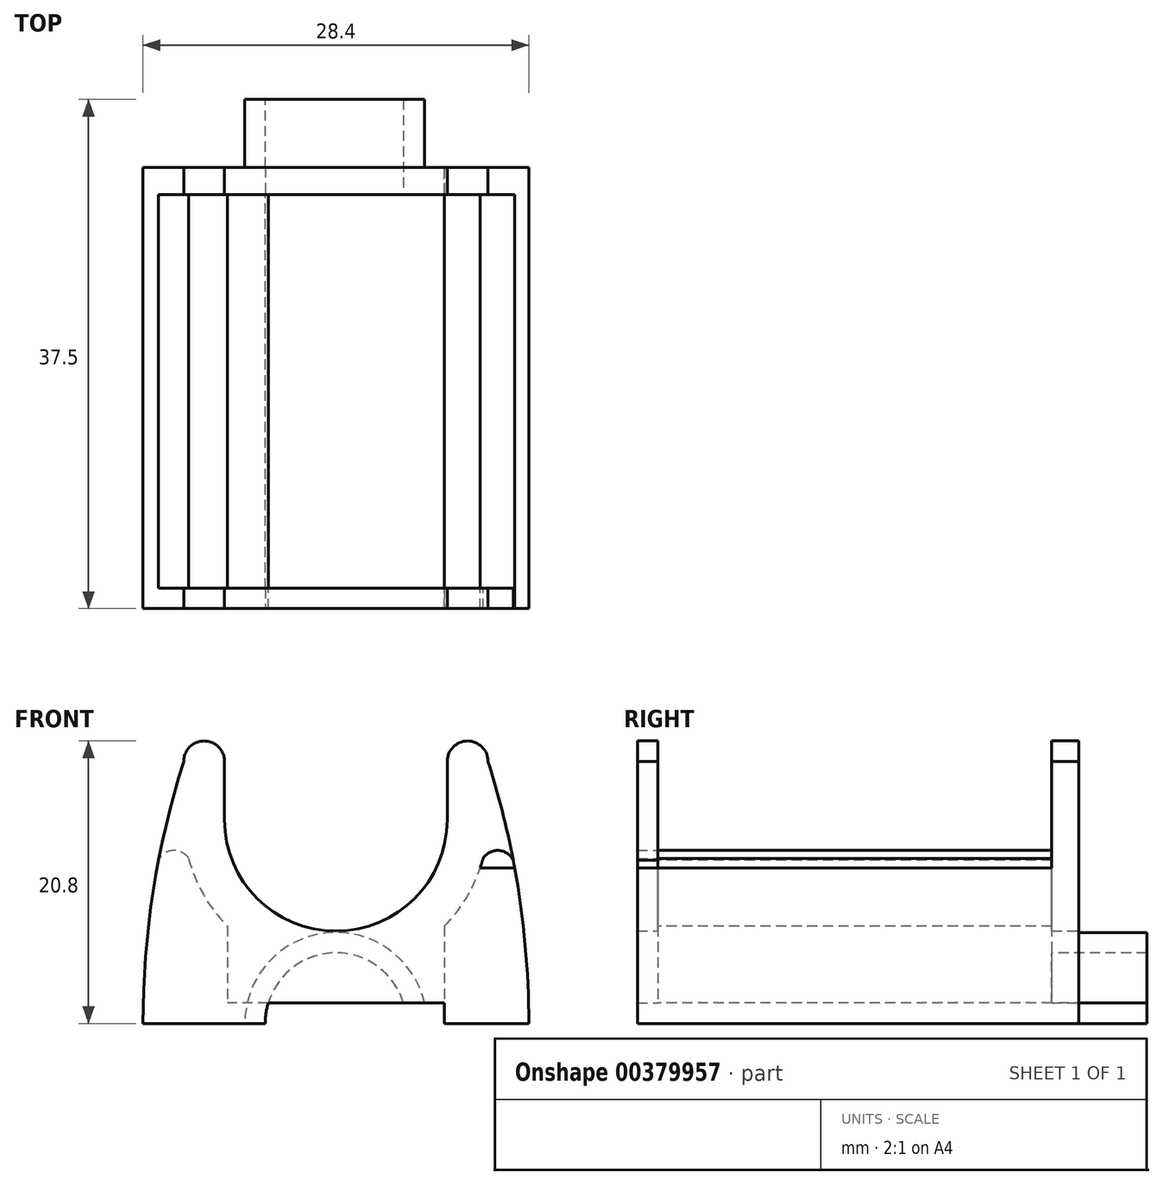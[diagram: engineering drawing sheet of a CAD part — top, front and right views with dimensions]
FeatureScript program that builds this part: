
annotation { "Feature Type Name" : "Feature", "Feature Type Description" : "" }
export const myFeature = defineFeature(function(context is Context, id is Id, definition is map)
    precondition{}
    {
        {
            var Q0;
            Q0=qCreatedBy(makeId("Front.planeOp"),FACE);
            cPlane(context, id + "F0", {"entities" : qUnion([Q0]), "cplaneType" : CPlaneType.OFFSET, "offset" : 6 * mm, "width" : 150 * mm, "height" : 150 * mm});
        }
        {
            var Q0;
            Q0=qCreatedBy(makeId("Front.planeOp"),FACE);
            cPlane(context, id + "F1", {"entities" : qUnion([Q0]), "cplaneType" : CPlaneType.OFFSET, "offset" : 37 * mm, "width" : 150 * mm, "height" : 150 * mm});
        }
        {
            var Q0;
            Q0=qCreatedBy(makeId("Top.planeOp"),FACE);
            var sketch = newSketch(context, id + "F2", { "sketchPlane" : qUnion([Q0])});
            skLineSegment(sketch, "E0.0", {"start": v(-8.05, -8) * mm, "end": v(-8.05, -37) * mm, "construction": true});
            skLineSegment(sketch, "E1.0", {"start": v(7.95, -8) * mm, "end": v(7.95, -37) * mm, "construction": true});
            skLineSegment(sketch, "E2.0", {"start": v(8.15, -8) * mm, "end": v(-8.25, -8) * mm, "construction": true});
            skLineSegment(sketch, "E3.0", {"start": v(8.15, -37) * mm, "end": v(-8.25, -37) * mm, "construction": true});
            skCircle(sketch, "E4", {"center": v(0, 0) * mm, "radius": 0.5 * mm, "construction": true});
            skLineSegment(sketch, "E5", {"start": v(-8.05, -22.5) * mm, "end": v(8.15, -8) * mm, "construction": true});
            skLineSegment(sketch, "E6", {"start": v(-8.05, -8) * mm, "end": v(7.95, -22.5) * mm, "construction": true});
            skLineSegment(sketch, "E7", {"start": v(7.95, -22.5) * mm, "end": v(-8.05, -37) * mm, "construction": true});
            skLineSegment(sketch, "E8", {"start": v(8.15, -37) * mm, "end": v(-8.05, -22.5) * mm, "construction": true});
            skCircle(sketch, "E9", {"center": v(0, -15.3) * mm, "radius": 1.38 * mm});
            skCircle(sketch, "E10", {"center": v(0, -29.7) * mm, "radius": 1.38 * mm});
            skSolve(sketch);
        }
        {
            var Q0;
            Q0=qCreatedBy(id+"F0.planeOp",FACE);
            var sketch = newSketch(context, id + "F3", { "sketchPlane" : qUnion([Q0])});
            skCircle(sketch, "E11", {"center": v(0, 0) * mm, "radius": 0.5 * mm, "construction": true});
            skArc(sketch, "E12.0", {"start": v(6.7, 8) * mm, "mid": v(0, 14.7) * mm, "end": v(-6.7, 8) * mm});
            skArc(sketch, "E13.0", {"start": v(5.2, 8) * mm, "mid": v(0, 13.2) * mm, "end": v(-5.2, 8) * mm});
            skLineSegment(sketch, "E14.bottom", {"start": v(14.2, 8) * mm, "end": v(-14.2, 8) * mm});
            skLineSegment(sketch, "E15", {"start": v(0, 23) * mm, "end": v(0, 8) * mm, "construction": true});
            skLineSegment(sketch, "E16", {"start": v(-8, 15.16) * mm, "end": v(-8, 8) * mm});
            skLineSegment(sketch, "E17.MirrorCS", {"start": v(8, 15.16) * mm, "end": v(8, 8) * mm});
            skLineSegment(sketch, "E18", {"start": v(-11.2, 23) * mm, "end": v(-11.2, 27.3) * mm});
            skLineSegment(sketch, "E19.MirrorCS", {"start": v(11.2, 23) * mm, "end": v(11.2, 27.3) * mm});
            skArc(sketch, "E20", {"start": v(-11.2, 23) * mm, "mid": v(-10.37, 18.77) * mm, "end": v(-8, 15.16) * mm});
            skLineSegment(sketch, "E21.0", {"start": v(8.2, 23) * mm, "end": v(8.2, 27.3) * mm});
            skLineSegment(sketch, "E22.MirrorCS", {"start": v(-8.2, 23) * mm, "end": v(-8.2, 27.3) * mm});
            skArc(sketch, "E23", {"start": v(8.2, 23) * mm, "mid": v(0, 14.8) * mm, "end": v(-8.2, 23) * mm});
            skArc(sketch, "E24.trimOffspring", {"start": v(8, 15.16) * mm, "mid": v(10.37, 18.77) * mm, "end": v(11.2, 23) * mm});
            skArc(sketch, "E25", {"start": v(-11.2, 27.3) * mm, "mid": v(-13.45, 17.77) * mm, "end": v(-14.2, 8) * mm});
            skArc(sketch, "E26", {"start": v(-11.2, 27.3) * mm, "mid": v(-9.7, 28.8) * mm, "end": v(-8.2, 27.3) * mm});
            skArc(sketch, "E27.MirrorCS", {"start": v(11.2, 27.3) * mm, "mid": v(13.45, 17.77) * mm, "end": v(14.2, 8) * mm});
            skArc(sketch, "E28.MirrorCS", {"start": v(11.2, 27.3) * mm, "mid": v(9.7, 28.8) * mm, "end": v(8.2, 27.3) * mm});
            skLineSegment(sketch, "E29.0", {"start": v(14.2, 9.5) * mm, "end": v(-14.2, 9.5) * mm});
            skSolve(sketch);
        }
        {
            var Q0;
            Q0=qCreatedBy(id+"F1.planeOp",FACE);
            var sketch = newSketch(context, id + "F4", { "sketchPlane" : qUnion([Q0])});
            skCircle(sketch, "E30", {"center": v(0, 0) * mm, "radius": 0.5 * mm, "construction": true});
            skArc(sketch, "E31.0", {"start": v(6.7, 8) * mm, "mid": v(0, 14.7) * mm, "end": v(-6.7, 8) * mm});
            skArc(sketch, "E32.0", {"start": v(5.2, 8) * mm, "mid": v(0, 13.2) * mm, "end": v(-5.2, 8) * mm});
            skLineSegment(sketch, "E33.bottom", {"start": v(14.2, 8) * mm, "end": v(-14.2, 8) * mm});
            skLineSegment(sketch, "E34", {"start": v(0, 23) * mm, "end": v(0, 8) * mm, "construction": true});
            skLineSegment(sketch, "E35", {"start": v(-8, 15.16) * mm, "end": v(-8, 8) * mm});
            skLineSegment(sketch, "E36.MirrorCS", {"start": v(8, 15.16) * mm, "end": v(8, 8) * mm});
            skLineSegment(sketch, "E37", {"start": v(-11.2, 23) * mm, "end": v(-11.2, 27.3) * mm});
            skLineSegment(sketch, "E38.MirrorCS", {"start": v(11.2, 23) * mm, "end": v(11.2, 27.3) * mm});
            skArc(sketch, "E39", {"start": v(-11.2, 23) * mm, "mid": v(-10.37, 18.77) * mm, "end": v(-8, 15.16) * mm});
            skLineSegment(sketch, "E40.0", {"start": v(8.2, 23) * mm, "end": v(8.2, 27.3) * mm});
            skLineSegment(sketch, "E41.MirrorCS", {"start": v(-8.2, 23) * mm, "end": v(-8.2, 27.3) * mm});
            skArc(sketch, "E42", {"start": v(8.2, 23) * mm, "mid": v(0, 14.8) * mm, "end": v(-8.2, 23) * mm});
            skArc(sketch, "E43.trimOffspring", {"start": v(8, 15.16) * mm, "mid": v(10.37, 18.77) * mm, "end": v(11.2, 23) * mm});
            skArc(sketch, "E44", {"start": v(-11.2, 27.3) * mm, "mid": v(-13.45, 17.77) * mm, "end": v(-14.2, 8) * mm});
            skArc(sketch, "E45", {"start": v(-11.2, 27.3) * mm, "mid": v(-9.7, 28.8) * mm, "end": v(-8.2, 27.3) * mm});
            skArc(sketch, "E46.MirrorCS", {"start": v(11.2, 27.3) * mm, "mid": v(13.45, 17.77) * mm, "end": v(14.2, 8) * mm});
            skArc(sketch, "E47.MirrorCS", {"start": v(11.2, 27.3) * mm, "mid": v(9.7, 28.8) * mm, "end": v(8.2, 27.3) * mm});
            skLineSegment(sketch, "E48.0", {"start": v(14.2, 9.5) * mm, "end": v(-14.2, 9.5) * mm});
            skLineSegment(sketch, "E49", {"start": v(10.33, 19.46) * mm, "end": v(13.34, 19.46) * mm});
            skLineSegment(sketch, "E50.MirrorCS", {"start": v(-10.33, 19.46) * mm, "end": v(-13.34, 19.46) * mm});
            skArc(sketch, "E51", {"start": v(10.63, 19.46) * mm, "mid": v(11.9, 20.74) * mm, "end": v(13.18, 19.46) * mm});
            skArc(sketch, "E52.MirrorCS", {"start": v(-10.63, 19.46) * mm, "mid": v(-11.9, 20.74) * mm, "end": v(-13.18, 19.46) * mm});
            skSolve(sketch);
        }
        {
            var Q0;
            {var subQ0=sQuery(id+"F3.wireOp",EDGE,"E12.0");Q0=makeQuery(id+"F3.imprint","IMPRINT",FACE,{"disambiguationData":[TD([[makeQuery(id+"F3.imprint","IMPRINT",EDGE,{"derivedFrom":subQ0}),1.0]])]});}
            var Q1;
            {var subQ0=sQuery(id+"F3.wireOp",EDGE,"E14.bottom");var subQ1=sQuery(id+"F3.wireOp",EDGE,"E13.0");var subQ2=makeQuery(id+"F3.imprint","INTERSECT",VERTEX,{"disambiguationData":[OD(0.0)],"derivedFrom":[subQ1,subQ0]});Q1=makeQuery(id+"F3.imprint","IMPRINT",FACE,{"disambiguationData":[TD([[makeQuery(id+"F3.imprint","IMPRINT",EDGE,{"disambiguationData":[TD([[subQ2,-1.0]])],"derivedFrom":subQ1}),1.0]])]});}
            extrude(context, id + "F5", {"entities" : qUnion([Q0, Q1]), "oppositeDirection" : true, "depth" : 5 * mm});
        }
        {
            var Q0;
            {var subQ1=sQuery(id+"F3.wireOp",EDGE,"E12.0");Q0=makeQuery(id+"F3.imprint","IMPRINT",FACE,{"disambiguationData":[TD([[makeQuery(id+"F3.imprint","IMPRINT",EDGE,{"derivedFrom":subQ1}),-1.0]])]});}
            var Q1;
            {var subQ0=sQuery(id+"F3.wireOp",EDGE,"E17.MirrorCS");Q1=makeQuery(id+"F3.imprint","IMPRINT",FACE,{"disambiguationData":[TD([[makeQuery(id+"F3.imprint","IMPRINT",EDGE,{"derivedFrom":subQ0}),1.0]])]});}
            var Q2;
            {var subQ0=sQuery(id+"F3.wireOp",EDGE,"E16");Q2=makeQuery(id+"F3.imprint","IMPRINT",FACE,{"disambiguationData":[TD([[makeQuery(id+"F3.imprint","IMPRINT",EDGE,{"derivedFrom":subQ0}),-1.0]])]});}
            var Q3;
            {var subQ0=sQuery(id+"F3.wireOp",EDGE,"E12.0");Q3=makeQuery(id+"F3.imprint","IMPRINT",FACE,{"disambiguationData":[TD([[makeQuery(id+"F3.imprint","IMPRINT",EDGE,{"derivedFrom":subQ0}),1.0]])]});}
            var Q4;
            {var subQ1=sQuery(id+"F3.wireOp",EDGE,"E19.MirrorCS");Q4=makeQuery(id+"F3.imprint","IMPRINT",FACE,{"disambiguationData":[TD([[makeQuery(id+"F3.imprint","IMPRINT",EDGE,{"derivedFrom":subQ1}),-1.0]])]});}
            var Q5;
            Q5=makeQuery(id+"F3.imprint","IMPRINT",FACE,{"disambiguationData":[TD([[makeQuery(id+"F3.imprint","IMPRINT",EDGE,{"derivedFrom":sQuery(id+"F3.wireOp",EDGE,"E18")}),-1.0]])]});
            var Q6;
            {var subQ1=sQuery(id+"F3.wireOp",EDGE,"E18");Q6=makeQuery(id+"F3.imprint","IMPRINT",FACE,{"disambiguationData":[TD([[makeQuery(id+"F3.imprint","IMPRINT",EDGE,{"derivedFrom":subQ1}),1.0]])]});}
            var Q7;
            {var subQ0=sQuery(id+"F3.wireOp",EDGE,"E14.bottom");var subQ1=sQuery(id+"F3.wireOp",EDGE,"E13.0");var subQ2=makeQuery(id+"F3.imprint","INTERSECT",VERTEX,{"disambiguationData":[OD(0.0)],"derivedFrom":[subQ1,subQ0]});Q7=makeQuery(id+"F3.imprint","IMPRINT",FACE,{"disambiguationData":[TD([[makeQuery(id+"F3.imprint","IMPRINT",EDGE,{"disambiguationData":[TD([[subQ2,-1.0]])],"derivedFrom":subQ1}),1.0]])]});}
            extrude(context, id + "F6", {"entities" : qUnion([Q0, Q1, Q2, Q3, Q4, Q5, Q6, Q7]), "operationType" : NewBodyOperationType.ADD, "depth" : 2 * mm});
        }
        {
            var Q0;
            {var subQ0=sQuery(id+"F4.wireOp",EDGE,"E46.MirrorCS");var subQ1=sQuery(id+"F4.wireOp",EDGE,"E33.bottom");var subQ2=makeQuery(id+"F4.imprint","INTERSECT",VERTEX,{"derivedFrom":[subQ1,subQ0]});Q0=makeQuery(id+"F4.imprint","IMPRINT",FACE,{"disambiguationData":[TD([[makeQuery(id+"F4.imprint","IMPRINT",EDGE,{"disambiguationData":[TD([[subQ2,-1.0]])],"derivedFrom":subQ1}),-1.0]])]});}
            var Q1;
            {var subQ0=sQuery(id+"F4.wireOp",EDGE,"E33.bottom");var subQ1=sQuery(id+"F4.wireOp",EDGE,"E31.0");var subQ2=makeQuery(id+"F4.imprint","INTERSECT",VERTEX,{"disambiguationData":[OD(0.0)],"derivedFrom":[subQ1,subQ0]});Q1=makeQuery(id+"F4.imprint","IMPRINT",FACE,{"disambiguationData":[TD([[makeQuery(id+"F4.imprint","IMPRINT",EDGE,{"disambiguationData":[TD([[subQ2,-1.0]])],"derivedFrom":subQ1}),-1.0]])]});}
            var Q2;
            {var subQ0=sQuery(id+"F4.wireOp",EDGE,"E33.bottom");var subQ1=sQuery(id+"F4.wireOp",EDGE,"E31.0");var subQ2=makeQuery(id+"F4.imprint","INTERSECT",VERTEX,{"disambiguationData":[OD(0.0)],"derivedFrom":[subQ1,subQ0]});Q2=makeQuery(id+"F4.imprint","IMPRINT",FACE,{"disambiguationData":[TD([[makeQuery(id+"F4.imprint","IMPRINT",EDGE,{"disambiguationData":[TD([[subQ2,-1.0]])],"derivedFrom":subQ1}),1.0]])]});}
            var Q3;
            {var subQ0=sQuery(id+"F4.wireOp",EDGE,"E33.bottom");var subQ1=sQuery(id+"F4.wireOp",EDGE,"E32.0");var subQ2=makeQuery(id+"F4.imprint","INTERSECT",VERTEX,{"disambiguationData":[OD(0.0)],"derivedFrom":[subQ1,subQ0]});Q3=makeQuery(id+"F4.imprint","IMPRINT",FACE,{"disambiguationData":[TD([[makeQuery(id+"F4.imprint","IMPRINT",EDGE,{"disambiguationData":[TD([[subQ2,-1.0]])],"derivedFrom":subQ1}),1.0]])]});}
            var Q4;
            {var subQ0=sQuery(id+"F4.wireOp",EDGE,"E33.bottom");var subQ1=sQuery(id+"F4.wireOp",EDGE,"E31.0");var subQ2=makeQuery(id+"F4.imprint","INTERSECT",VERTEX,{"disambiguationData":[OD(1.0)],"derivedFrom":[subQ1,subQ0]});Q4=makeQuery(id+"F4.imprint","IMPRINT",FACE,{"disambiguationData":[TD([[makeQuery(id+"F4.imprint","IMPRINT",EDGE,{"disambiguationData":[TD([[subQ2,1.0]])],"derivedFrom":subQ1}),1.0]])]});}
            var Q5;
            {var subQ0=sQuery(id+"F4.wireOp",EDGE,"E33.bottom");var subQ1=sQuery(id+"F4.wireOp",EDGE,"E31.0");var subQ2=makeQuery(id+"F4.imprint","INTERSECT",VERTEX,{"disambiguationData":[OD(1.0)],"derivedFrom":[subQ1,subQ0]});Q5=makeQuery(id+"F4.imprint","IMPRINT",FACE,{"disambiguationData":[TD([[makeQuery(id+"F4.imprint","IMPRINT",EDGE,{"disambiguationData":[TD([[subQ2,1.0]])],"derivedFrom":subQ1}),-1.0]])]});}
            var Q6;
            {var subQ0=sQuery(id+"F4.wireOp",EDGE,"E44");var subQ1=sQuery(id+"F4.wireOp",EDGE,"E33.bottom");var subQ2=makeQuery(id+"F4.imprint","INTERSECT",VERTEX,{"derivedFrom":[subQ1,subQ0]});Q6=makeQuery(id+"F4.imprint","IMPRINT",FACE,{"disambiguationData":[TD([[makeQuery(id+"F4.imprint","IMPRINT",EDGE,{"disambiguationData":[TD([[subQ2,1.0]])],"derivedFrom":subQ1}),-1.0]])]});}
            var Q7;
            {var subQ5=sQuery(id+"F4.wireOp",EDGE,"E35");var subQ7=sQuery(id+"F4.wireOp",EDGE,"E39");var subQ8=makeQuery(id+"F4.imprint","INTERSECT",VERTEX,{"derivedFrom":[subQ5,subQ7]});Q7=makeQuery(id+"F4.imprint","IMPRINT",FACE,{"disambiguationData":[TD([[makeQuery(id+"F4.imprint","IMPRINT",EDGE,{"disambiguationData":[TD([[subQ8,-1.0]])],"derivedFrom":subQ5}),-1.0]])]});}
            var Q8;
            {var subQ5=sQuery(id+"F4.wireOp",EDGE,"E36.MirrorCS");var subQ7=sQuery(id+"F4.wireOp",EDGE,"E43.trimOffspring");var subQ8=makeQuery(id+"F4.imprint","INTERSECT",VERTEX,{"derivedFrom":[subQ5,subQ7]});Q8=makeQuery(id+"F4.imprint","IMPRINT",FACE,{"disambiguationData":[TD([[makeQuery(id+"F4.imprint","IMPRINT",EDGE,{"disambiguationData":[TD([[subQ8,-1.0]])],"derivedFrom":subQ5}),1.0]])]});}
            var Q9;
            {var subQ0=sQuery(id+"F4.wireOp",EDGE,"E51");var subQ5=sQuery(id+"F4.wireOp",EDGE,"E46.MirrorCS");var subQ6=makeQuery(id+"F4.imprint","INTERSECT",VERTEX,{"derivedFrom":[subQ5,subQ0]});Q9=makeQuery(id+"F4.imprint","IMPRINT",FACE,{"disambiguationData":[TD([[makeQuery(id+"F4.imprint","IMPRINT",EDGE,{"disambiguationData":[TD([[subQ6,-1.0]])],"derivedFrom":subQ5}),-1.0]])]});}
            var Q10;
            {var subQ0=sQuery(id+"F4.wireOp",EDGE,"E52.MirrorCS");var subQ5=sQuery(id+"F4.wireOp",EDGE,"E44");var subQ6=makeQuery(id+"F4.imprint","INTERSECT",VERTEX,{"derivedFrom":[subQ5,subQ0]});Q10=makeQuery(id+"F4.imprint","IMPRINT",FACE,{"disambiguationData":[TD([[makeQuery(id+"F4.imprint","IMPRINT",EDGE,{"disambiguationData":[TD([[subQ6,-1.0]])],"derivedFrom":subQ5}),1.0]])]});}
            extrude(context, id + "F7", {"entities" : qUnion([Q0, Q1, Q2, Q3, Q4, Q5, Q6, Q7, Q8, Q9, Q10]), "operationType" : NewBodyOperationType.ADD, "oppositeDirection" : true, "depth" : 29 * mm});
        }
        {
            var Q0;
            {var subQ0=sQuery(id+"F4.wireOp",EDGE,"E37");Q0=makeQuery(id+"F4.imprint","IMPRINT",FACE,{"disambiguationData":[TD([[makeQuery(id+"F4.imprint","IMPRINT",EDGE,{"derivedFrom":subQ0}),1.0]])]});}
            var Q1;
            {var subQ0=sQuery(id+"F4.wireOp",EDGE,"E52.MirrorCS");var subQ5=sQuery(id+"F4.wireOp",EDGE,"E44");var subQ6=makeQuery(id+"F4.imprint","INTERSECT",VERTEX,{"derivedFrom":[subQ5,subQ0]});Q1=makeQuery(id+"F4.imprint","IMPRINT",FACE,{"disambiguationData":[TD([[makeQuery(id+"F4.imprint","IMPRINT",EDGE,{"disambiguationData":[TD([[subQ6,-1.0]])],"derivedFrom":subQ5}),1.0]])]});}
            var Q2;
            {var subQ3=sQuery(id+"F4.wireOp",EDGE,"E35");var subQ7=sQuery(id+"F4.wireOp",EDGE,"E39");var subQ8=makeQuery(id+"F4.imprint","INTERSECT",VERTEX,{"derivedFrom":[subQ3,subQ7]});Q2=makeQuery(id+"F4.imprint","IMPRINT",FACE,{"disambiguationData":[TD([[makeQuery(id+"F4.imprint","IMPRINT",EDGE,{"disambiguationData":[TD([[subQ8,-1.0]])],"derivedFrom":subQ3}),-1.0]])]});}
            var Q3;
            {var subQ0=sQuery(id+"F4.wireOp",EDGE,"E44");var subQ1=sQuery(id+"F4.wireOp",EDGE,"E33.bottom");var subQ2=makeQuery(id+"F4.imprint","INTERSECT",VERTEX,{"derivedFrom":[subQ1,subQ0]});Q3=makeQuery(id+"F4.imprint","IMPRINT",FACE,{"disambiguationData":[TD([[makeQuery(id+"F4.imprint","IMPRINT",EDGE,{"disambiguationData":[TD([[subQ2,1.0]])],"derivedFrom":subQ1}),-1.0]])]});}
            var Q4;
            {var subQ5=sQuery(id+"F4.wireOp",EDGE,"E37");Q4=makeQuery(id+"F4.imprint","IMPRINT",FACE,{"disambiguationData":[TD([[makeQuery(id+"F4.imprint","IMPRINT",EDGE,{"derivedFrom":subQ5}),-1.0]])]});}
            var Q5;
            {var subQ0=sQuery(id+"F4.wireOp",EDGE,"E38.MirrorCS");Q5=makeQuery(id+"F4.imprint","IMPRINT",FACE,{"disambiguationData":[TD([[makeQuery(id+"F4.imprint","IMPRINT",EDGE,{"derivedFrom":subQ0}),-1.0]])]});}
            var Q6;
            {var subQ3=sQuery(id+"F4.wireOp",EDGE,"E36.MirrorCS");var subQ7=sQuery(id+"F4.wireOp",EDGE,"E43.trimOffspring");var subQ8=makeQuery(id+"F4.imprint","INTERSECT",VERTEX,{"derivedFrom":[subQ3,subQ7]});Q6=makeQuery(id+"F4.imprint","IMPRINT",FACE,{"disambiguationData":[TD([[makeQuery(id+"F4.imprint","IMPRINT",EDGE,{"disambiguationData":[TD([[subQ8,-1.0]])],"derivedFrom":subQ3}),1.0]])]});}
            var Q7;
            {var subQ0=sQuery(id+"F4.wireOp",EDGE,"E46.MirrorCS");var subQ1=sQuery(id+"F4.wireOp",EDGE,"E33.bottom");var subQ2=makeQuery(id+"F4.imprint","INTERSECT",VERTEX,{"derivedFrom":[subQ1,subQ0]});Q7=makeQuery(id+"F4.imprint","IMPRINT",FACE,{"disambiguationData":[TD([[makeQuery(id+"F4.imprint","IMPRINT",EDGE,{"disambiguationData":[TD([[subQ2,-1.0]])],"derivedFrom":subQ1}),-1.0]])]});}
            var Q8;
            {var subQ0=sQuery(id+"F4.wireOp",EDGE,"E33.bottom");var subQ1=sQuery(id+"F4.wireOp",EDGE,"E31.0");var subQ2=makeQuery(id+"F4.imprint","INTERSECT",VERTEX,{"disambiguationData":[OD(0.0)],"derivedFrom":[subQ1,subQ0]});Q8=makeQuery(id+"F4.imprint","IMPRINT",FACE,{"disambiguationData":[TD([[makeQuery(id+"F4.imprint","IMPRINT",EDGE,{"disambiguationData":[TD([[subQ2,-1.0]])],"derivedFrom":subQ1}),-1.0]])]});}
            var Q9;
            {var subQ0=sQuery(id+"F4.wireOp",EDGE,"E33.bottom");var subQ1=sQuery(id+"F4.wireOp",EDGE,"E31.0");var subQ2=makeQuery(id+"F4.imprint","INTERSECT",VERTEX,{"disambiguationData":[OD(0.0)],"derivedFrom":[subQ1,subQ0]});Q9=makeQuery(id+"F4.imprint","IMPRINT",FACE,{"disambiguationData":[TD([[makeQuery(id+"F4.imprint","IMPRINT",EDGE,{"disambiguationData":[TD([[subQ2,-1.0]])],"derivedFrom":subQ1}),1.0]])]});}
            var Q10;
            {var subQ0=sQuery(id+"F4.wireOp",EDGE,"E48.0");var subQ1=sQuery(id+"F4.wireOp",EDGE,"E31.0");var subQ2=makeQuery(id+"F4.imprint","INTERSECT",VERTEX,{"disambiguationData":[OD(0.0)],"derivedFrom":[subQ1,subQ0]});Q10=makeQuery(id+"F4.imprint","IMPRINT",FACE,{"disambiguationData":[TD([[makeQuery(id+"F4.imprint","IMPRINT",EDGE,{"disambiguationData":[TD([[subQ2,-1.0]])],"derivedFrom":subQ1}),1.0]])]});}
            var Q11;
            {var subQ0=sQuery(id+"F4.wireOp",EDGE,"E33.bottom");var subQ1=sQuery(id+"F4.wireOp",EDGE,"E31.0");var subQ2=makeQuery(id+"F4.imprint","INTERSECT",VERTEX,{"disambiguationData":[OD(1.0)],"derivedFrom":[subQ1,subQ0]});Q11=makeQuery(id+"F4.imprint","IMPRINT",FACE,{"disambiguationData":[TD([[makeQuery(id+"F4.imprint","IMPRINT",EDGE,{"disambiguationData":[TD([[subQ2,1.0]])],"derivedFrom":subQ1}),1.0]])]});}
            var Q12;
            {var subQ0=sQuery(id+"F4.wireOp",EDGE,"E33.bottom");var subQ1=sQuery(id+"F4.wireOp",EDGE,"E31.0");var subQ2=makeQuery(id+"F4.imprint","INTERSECT",VERTEX,{"disambiguationData":[OD(1.0)],"derivedFrom":[subQ1,subQ0]});Q12=makeQuery(id+"F4.imprint","IMPRINT",FACE,{"disambiguationData":[TD([[makeQuery(id+"F4.imprint","IMPRINT",EDGE,{"disambiguationData":[TD([[subQ2,1.0]])],"derivedFrom":subQ1}),-1.0]])]});}
            var Q13;
            {var subQ0=sQuery(id+"F4.wireOp",EDGE,"E33.bottom");var subQ1=sQuery(id+"F4.wireOp",EDGE,"E32.0");var subQ2=makeQuery(id+"F4.imprint","INTERSECT",VERTEX,{"disambiguationData":[OD(0.0)],"derivedFrom":[subQ1,subQ0]});Q13=makeQuery(id+"F4.imprint","IMPRINT",FACE,{"disambiguationData":[TD([[makeQuery(id+"F4.imprint","IMPRINT",EDGE,{"disambiguationData":[TD([[subQ2,-1.0]])],"derivedFrom":subQ1}),1.0]])]});}
            var Q14;
            {var subQ0=sQuery(id+"F4.wireOp",EDGE,"E48.0");var subQ1=sQuery(id+"F4.wireOp",EDGE,"E32.0");var subQ2=makeQuery(id+"F4.imprint","INTERSECT",VERTEX,{"disambiguationData":[OD(0.0)],"derivedFrom":[subQ1,subQ0]});Q14=makeQuery(id+"F4.imprint","IMPRINT",FACE,{"disambiguationData":[TD([[makeQuery(id+"F4.imprint","IMPRINT",EDGE,{"disambiguationData":[TD([[subQ2,-1.0]])],"derivedFrom":subQ1}),1.0]])]});}
            var Q15;
            {var subQ0=sQuery(id+"F4.wireOp",EDGE,"E51");var subQ5=sQuery(id+"F4.wireOp",EDGE,"E46.MirrorCS");var subQ6=makeQuery(id+"F4.imprint","INTERSECT",VERTEX,{"derivedFrom":[subQ5,subQ0]});Q15=makeQuery(id+"F4.imprint","IMPRINT",FACE,{"disambiguationData":[TD([[makeQuery(id+"F4.imprint","IMPRINT",EDGE,{"disambiguationData":[TD([[subQ6,-1.0]])],"derivedFrom":subQ5}),-1.0]])]});}
            var Q16;
            {var subQ0=sQuery(id+"F4.wireOp",EDGE,"E51");var subQ1=sQuery(id+"F4.wireOp",EDGE,"E43.trimOffspring");var subQ3=makeQuery(id+"F4.imprint","INTERSECT",VERTEX,{"derivedFrom":[subQ1,subQ0]});Q16=makeQuery(id+"F4.imprint","IMPRINT",FACE,{"disambiguationData":[TD([[makeQuery(id+"F4.imprint","IMPRINT",EDGE,{"disambiguationData":[TD([[subQ3,1.0]])],"derivedFrom":subQ1}),1.0]])]});}
            var Q17;
            {var subQ0=sQuery(id+"F4.wireOp",EDGE,"E52.MirrorCS");var subQ1=sQuery(id+"F4.wireOp",EDGE,"E39");var subQ3=makeQuery(id+"F4.imprint","INTERSECT",VERTEX,{"derivedFrom":[subQ1,subQ0]});Q17=makeQuery(id+"F4.imprint","IMPRINT",FACE,{"disambiguationData":[TD([[makeQuery(id+"F4.imprint","IMPRINT",EDGE,{"disambiguationData":[TD([[subQ3,-1.0]])],"derivedFrom":subQ1}),1.0]])]});}
            extrude(context, id + "F8", {"entities" : qUnion([Q0, Q1, Q2, Q3, Q4, Q5, Q6, Q7, Q8, Q9, Q10, Q11, Q12, Q13, Q14, Q15, Q16, Q17]), "operationType" : NewBodyOperationType.ADD, "depth" : 1.5 * mm});
        }
        {
            var Q0;
            Q0=sQuery(id+"F2.wireOp",VERTEX,"E9.center");
            var Q1;
            Q1=sQuery(id+"F2.wireOp",VERTEX,"E10.center");
            var Q2;
            Q2=makeQuery(id+"F5.opExtrude","SWEPT_BODY",BODY,{"disambiguationData":[OSD([sQuery(id+"F3.wireOp",EDGE,"E12.0"),sQuery(id+"F3.wireOp",EDGE,"E13.0"),sQuery(id+"F3.wireOp",EDGE,"E14.bottom"),sQuery(id+"F3.wireOp",EDGE,"E29.0")])]});
            hole(context, id + "F9", {"style" : HoleStyle.SIMPLE, "endStyle" : HoleEndStyle.THROUGH, "oppositeDirection" : true, "holeDiameter" : 2.75 * mm, "isTappedThrough" : true, "tappedDepth" : 12 * mm, "tapClearance" : 3, "startFromSketch" : true, "locations" : qUnion([Q0, Q1]), "scope" : qUnion([Q2])});
        }
    });
